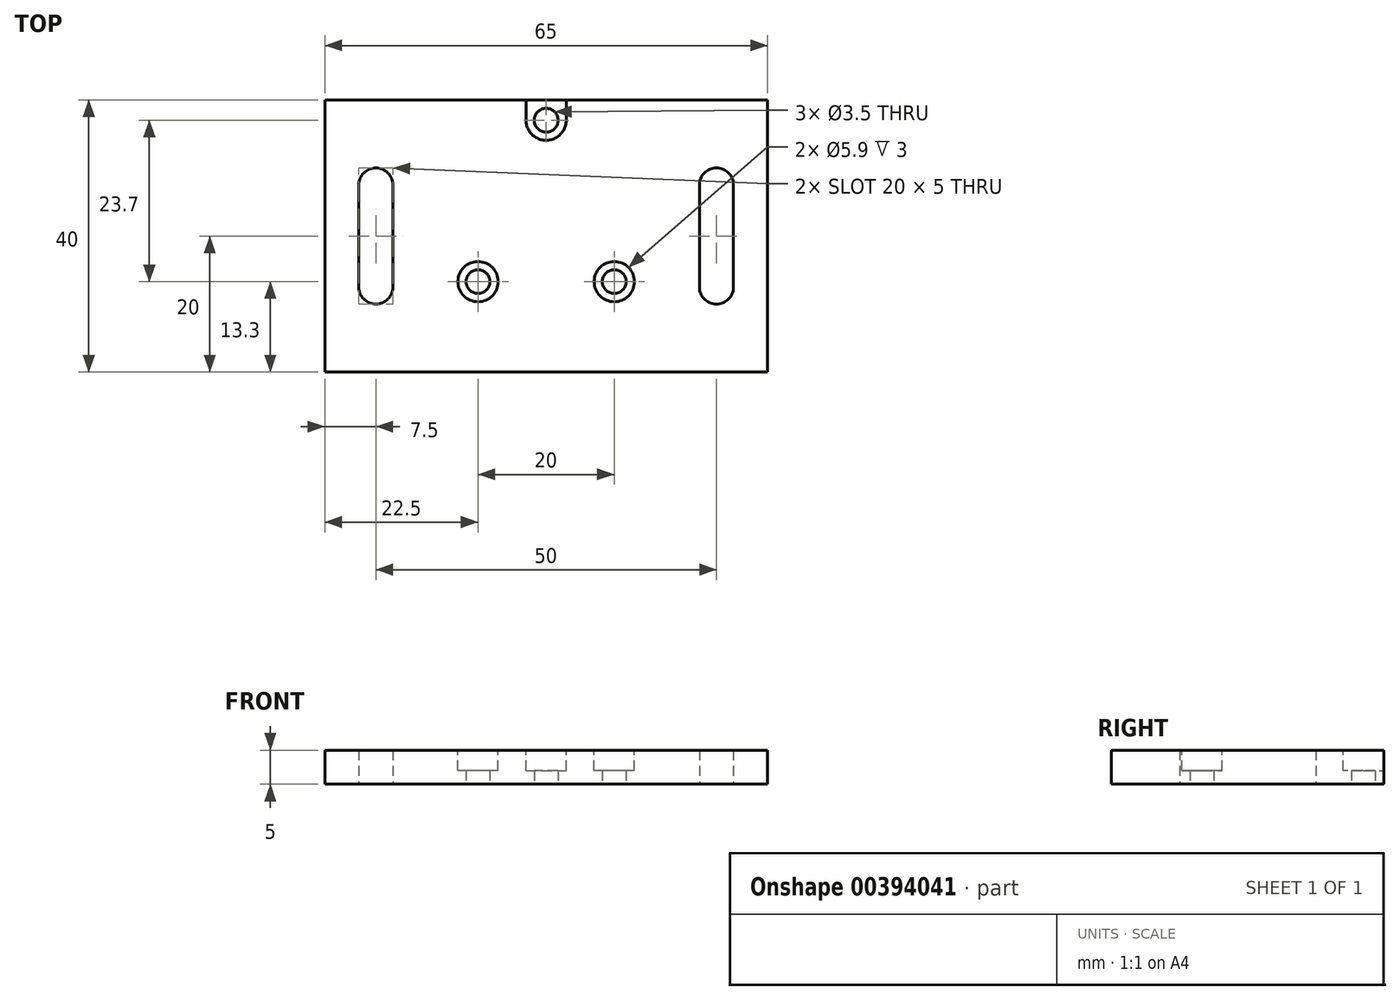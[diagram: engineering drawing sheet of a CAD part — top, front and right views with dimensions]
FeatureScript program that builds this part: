
annotation { "Feature Type Name" : "Feature", "Feature Type Description" : "" }
export const myFeature = defineFeature(function(context is Context, id is Id, definition is map)
    precondition{}
    {
        {
            var Q0;
            Q0=qCreatedBy(makeId("Top.planeOp"),FACE);
            var sketch = newSketch(context, id + "F0", { "sketchPlane" : qUnion([Q0])});
            skLineSegment(sketch, "E0.bottom", {"start": v(-32.5, 20) * mm, "end": v(32.5, 20) * mm});
            skLineSegment(sketch, "E0.top", {"start": v(-32.5, -20) * mm, "end": v(32.5, -20) * mm});
            skLineSegment(sketch, "E0.left", {"start": v(-32.5, 20) * mm, "end": v(-32.5, -20) * mm});
            skLineSegment(sketch, "E0.right", {"start": v(32.5, 20) * mm, "end": v(32.5, -20) * mm});
            skCircle(sketch, "E1", {"center": v(0, 17) * mm, "radius": 1.75 * mm});
            skCircle(sketch, "E2", {"center": v(-10, -6.7) * mm, "radius": 1.75 * mm});
            skCircle(sketch, "E3", {"center": v(10, -6.7) * mm, "radius": 1.75 * mm});
            skArc(sketch, "E4", {"start": v(-27.5, -7.5) * mm, "mid": v(-25, -10) * mm, "end": v(-22.5, -7.5) * mm});
            skArc(sketch, "E5", {"start": v(22.5, -7.5) * mm, "mid": v(25, -10) * mm, "end": v(27.5, -7.5) * mm});
            skArc(sketch, "E6", {"start": v(-22.5, 7.5) * mm, "mid": v(-25, 10) * mm, "end": v(-27.5, 7.5) * mm});
            skArc(sketch, "E7", {"start": v(27.5, 7.5) * mm, "mid": v(25, 10) * mm, "end": v(22.5, 7.5) * mm});
            skLineSegment(sketch, "E8", {"start": v(-22.5, 7.5) * mm, "end": v(-22.5, -7.5) * mm});
            skLineSegment(sketch, "E9", {"start": v(-27.5, 7.5) * mm, "end": v(-27.5, -7.5) * mm});
            skLineSegment(sketch, "E10", {"start": v(22.5, 7.5) * mm, "end": v(22.5, -7.5) * mm});
            skLineSegment(sketch, "E11", {"start": v(27.5, 7.5) * mm, "end": v(27.5, -7.5) * mm});
            skSolve(sketch);
        }
        {
            var Q0;
            Q0 = qSketchRegion(id + "F0", true);
            extrude(context, id + "F1", {"entities" : qUnion([Q0]), "depth" : 5 * mm});
        }
        {
            var Q0;
            Q0=makeQuery(id+"F1.opExtrude","CAP_FACE",FACE,{"disambiguationData":[OSD([sQuery(id+"F0.wireOp",EDGE,"E0.bottom"),sQuery(id+"F0.wireOp",EDGE,"E0.top"),sQuery(id+"F0.wireOp",EDGE,"E0.left"),sQuery(id+"F0.wireOp",EDGE,"E0.right"),sQuery(id+"F0.wireOp",EDGE,"E1"),sQuery(id+"F0.wireOp",EDGE,"E2"),sQuery(id+"F0.wireOp",EDGE,"E3"),sQuery(id+"F0.wireOp",EDGE,"E4"),sQuery(id+"F0.wireOp",EDGE,"E5")])],"isStart":false});
            var sketch = newSketch(context, id + "F2", { "sketchPlane" : qUnion([Q0])});
            skCircle(sketch, "E12", {"center": v(-10, -6.7) * mm, "radius": 2.95 * mm});
            skCircle(sketch, "E13", {"center": v(10, -6.7) * mm, "radius": 2.95 * mm});
            skArc(sketch, "E14", {"start": v(-2.95, 17.02) * mm, "mid": v(0, 14.05) * mm, "end": v(2.95, 17.02) * mm});
            skLineSegment(sketch, "E15.bottom", {"start": v(2.95, 17.02) * mm, "end": v(2.95, 17.02) * mm});
            skLineSegment(sketch, "E15.top", {"start": v(-2.95, 20) * mm, "end": v(2.95, 20) * mm});
            skLineSegment(sketch, "E15.left", {"start": v(-2.95, 17.02) * mm, "end": v(-2.95, 20) * mm});
            skLineSegment(sketch, "E15.right", {"start": v(2.95, 17.02) * mm, "end": v(2.95, 20) * mm});
            skSolve(sketch);
        }
        {
            var Q0;
            Q0=makeQuery(id+"F2.imprint","IMPRINT",FACE,{"disambiguationData":[TD([[makeQuery(id+"F2.imprint","IMPRINT",EDGE,{"derivedFrom":sQuery(id+"F2.wireOp",EDGE,"E13")}),1.0]])]});
            var Q1;
            Q1=makeQuery(id+"F2.imprint","IMPRINT",FACE,{"disambiguationData":[TD([[makeQuery(id+"F2.imprint","IMPRINT",EDGE,{"derivedFrom":makeQuery(id+"F1.opExtrude","CAP_EDGE",EDGE,{"disambiguationData":[OSD([sQuery(id+"F0.wireOp",EDGE,"E2")])],"isStart":false})}),1.0]])]});
            var Q2;
            Q2=makeQuery(id+"F2.imprint","IMPRINT",FACE,{"disambiguationData":[TD([[makeQuery(id+"F2.imprint","IMPRINT",EDGE,{"derivedFrom":sQuery(id+"F2.wireOp",EDGE,"E12")}),1.0]])]});
            var Q3;
            Q3=makeQuery(id+"F2.imprint","IMPRINT",FACE,{"disambiguationData":[TD([[makeQuery(id+"F2.imprint","IMPRINT",EDGE,{"derivedFrom":sQuery(id+"F2.wireOp",EDGE,"E14")}),1.0]])]});
            extrude(context, id + "F3", {"entities" : qUnion([Q0, Q1, Q2, Q3]), "operationType" : NewBodyOperationType.REMOVE, "oppositeDirection" : true, "depth" : 3 * mm});
        }
    });
